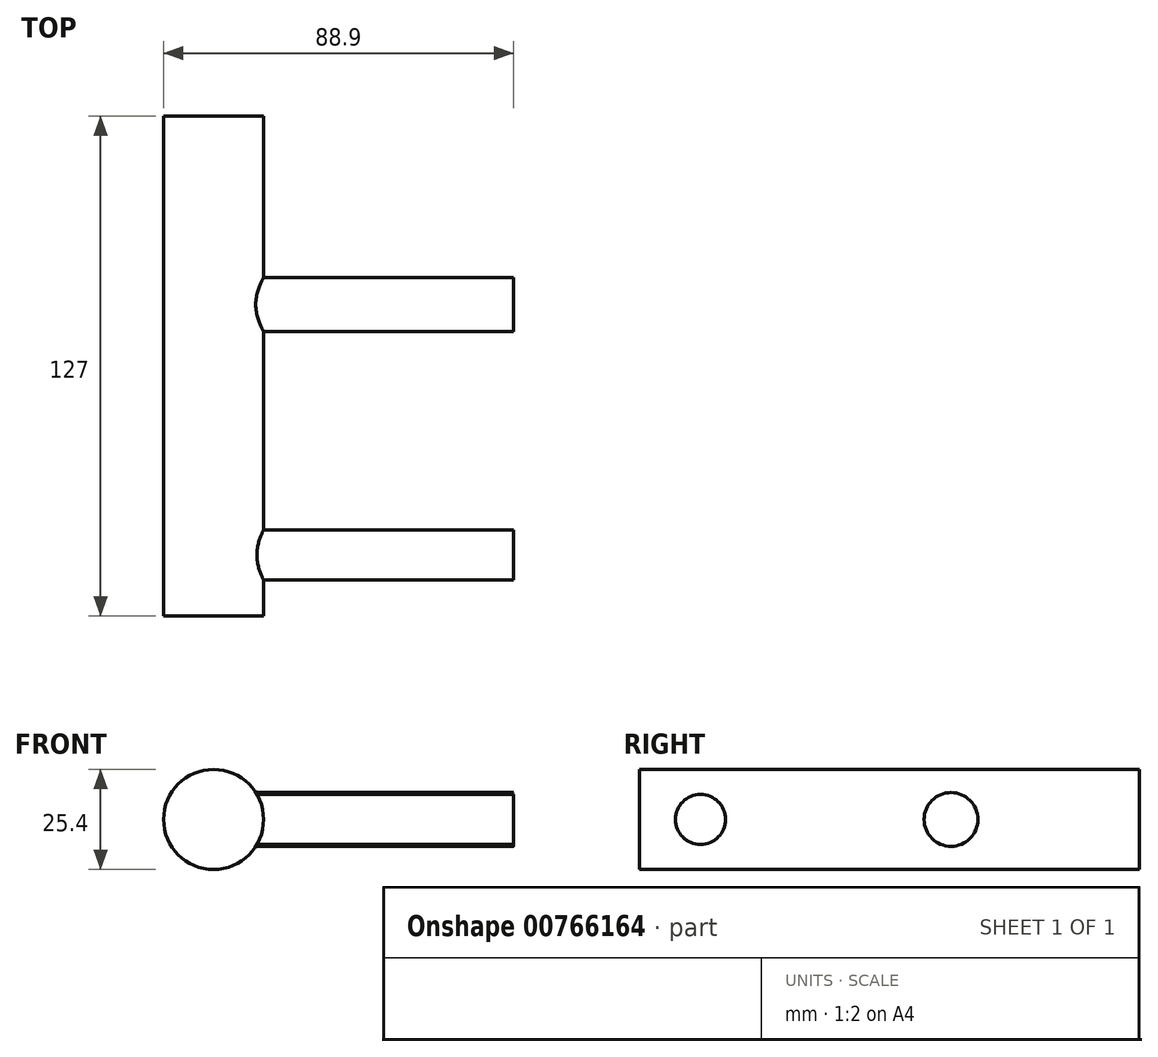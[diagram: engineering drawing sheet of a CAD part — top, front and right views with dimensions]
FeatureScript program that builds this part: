
annotation { "Feature Type Name" : "Feature", "Feature Type Description" : "" }
export const myFeature = defineFeature(function(context is Context, id is Id, definition is map)
    precondition{}
    {
        {
            var Q0;
            Q0=qCreatedBy(makeId("Front.planeOp"),FACE);
            var sketch = newSketch(context, id + "F0", { "sketchPlane" : qUnion([Q0])});
            skCircle(sketch, "E0", {"center": v(0, 0) * mm, "radius": 12.7 * mm});
            skSolve(sketch);
        }
        {
            var Q0;
            Q0 = qSketchRegion(id + "F0", true);
            extrude(context, id + "F1", {"entities" : qUnion([Q0]), "oppositeDirection" : true, "depth" : 127 * mm, "offsetDistance" : 25.4 * mm});
        }
        {
            var Q0;
            Q0=qCreatedBy(makeId("Right.planeOp"),FACE);
            var sketch = newSketch(context, id + "F2", { "sketchPlane" : qUnion([Q0])});
            skCircle(sketch, "E1", {"center": v(15.5, 0) * mm, "radius": 6.35 * mm});
            skCircle(sketch, "E2", {"center": v(79.13, 0) * mm, "radius": 6.83 * mm});
            skSolve(sketch);
        }
        {
            var Q0;
            Q0 = qSketchRegion(id + "F2", true);
            extrude(context, id + "F3", {"entities" : qUnion([Q0]), "operationType" : NewBodyOperationType.ADD, "depth" : 76.2 * mm, "offsetDistance" : 25.4 * mm});
        }
    });
